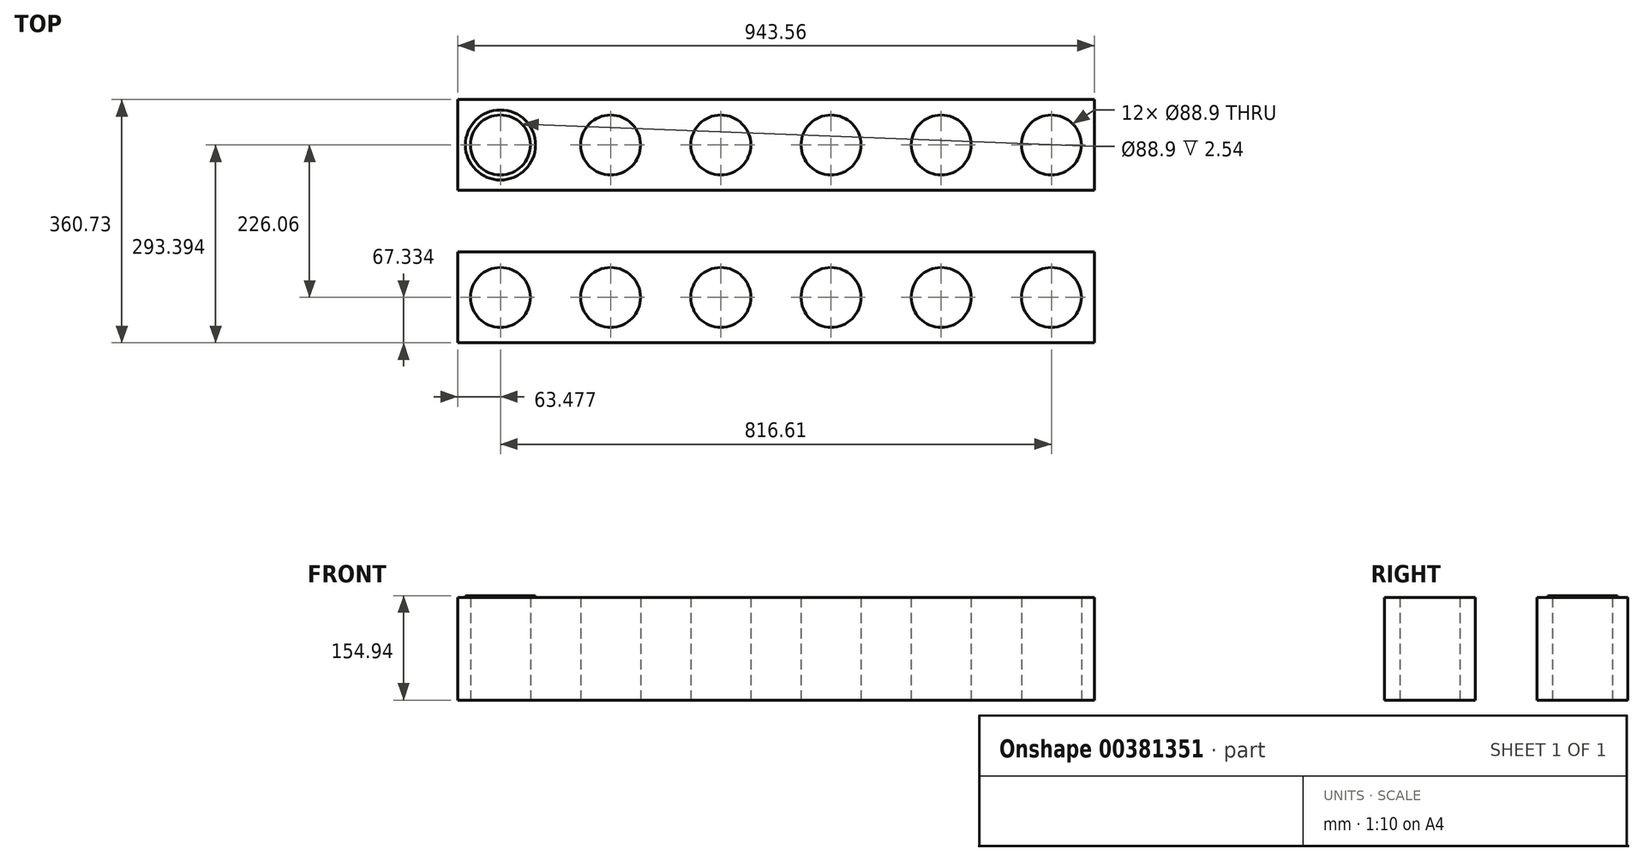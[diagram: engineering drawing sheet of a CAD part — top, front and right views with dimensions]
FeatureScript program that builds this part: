
annotation { "Feature Type Name" : "Feature", "Feature Type Description" : "" }
export const myFeature = defineFeature(function(context is Context, id is Id, definition is map)
    precondition{}
    {
        {
            var Q0;
            Q0=qCreatedBy(makeId("Top.planeOp"),FACE);
            var sketch = newSketch(context, id + "F0", { "sketchPlane" : qUnion([Q0])});
            skCircle(sketch, "E0", {"center": v(-123, 5.68) * mm, "radius": 44.45 * mm});
            skLineSegment(sketch, "E1", {"start": v(-123, 5.68) * mm, "end": v(203.64, 5.68) * mm});
            skCircle(sketch, "E2", {"center": v(40.32, 5.68) * mm, "radius": 44.45 * mm});
            skCircle(sketch, "E3", {"center": v(203.64, 5.68) * mm, "radius": 44.45 * mm});
            skLineSegment(sketch, "E4", {"start": v(366.96, 5.68) * mm, "end": v(640.3, 5.68) * mm});
            skCircle(sketch, "E5", {"center": v(366.96, 5.68) * mm, "radius": 44.45 * mm});
            skCircle(sketch, "E6", {"center": v(530.29, 5.68) * mm, "radius": 44.45 * mm});
            skLineSegment(sketch, "E7", {"start": v(640.3, 5.68) * mm, "end": v(693.6, 5.68) * mm});
            skCircle(sketch, "E8", {"center": v(693.6, 5.68) * mm, "radius": 44.45 * mm});
            skLineSegment(sketch, "E9", {"start": v(203.64, 5.68) * mm, "end": v(366.96, 5.68) * mm});
            skLineSegment(sketch, "E10.bottom", {"start": v(757.08, -61.65) * mm, "end": v(-186.48, -61.65) * mm});
            skLineSegment(sketch, "E10.top", {"start": v(757.08, 73.02) * mm, "end": v(-186.48, 73.02) * mm});
            skLineSegment(sketch, "E10.left", {"start": v(757.08, -61.65) * mm, "end": v(757.08, 73.02) * mm});
            skLineSegment(sketch, "E10.right", {"start": v(-186.48, -61.65) * mm, "end": v(-186.48, 73.02) * mm});
            skPoint(sketch, "E10.middle", {"position": v(285.3, 5.68) * mm});
            skSolve(sketch);
        }
        {
            var Q0;
            Q0 = qSketchRegion(id + "F0", true);
            extrude(context, id + "F1", {"entities" : qUnion([Q0]), "depth" : 152.4 * mm});
        }
        {
            var Q0;
            Q0=makeQuery(id+"F1.opExtrude","SWEPT_BODY",BODY,{"disambiguationData":[OSD([sQuery(id+"F0.wireOp",EDGE,"E0"),sQuery(id+"F0.wireOp",EDGE,"E2"),sQuery(id+"F0.wireOp",EDGE,"E3"),sQuery(id+"F0.wireOp",EDGE,"E5"),sQuery(id+"F0.wireOp",EDGE,"E6"),sQuery(id+"F0.wireOp",EDGE,"E8"),sQuery(id+"F0.wireOp",EDGE,"E10.bottom"),sQuery(id+"F0.wireOp",EDGE,"E10.top"),sQuery(id+"F0.wireOp",EDGE,"E10.left"),sQuery(id+"F0.wireOp",EDGE,"E10.right")])]});
            transform(context, id + "F2", {"entities" : qUnion([Q0]), "transformType" : TransformType.TRANSLATION_3D, "dx" : 0 * mm, "dy" : 226.06 * mm, "dz" : 0 * mm, "makeCopy" : true});
        }
        {
            var Q0;
            Q0=makeQuery(id+"F2.opPattern","COPY",FACE,{"derivedFrom":makeQuery(id+"F1.opExtrude","CAP_FACE",FACE,{"disambiguationData":[OSD([sQuery(id+"F0.wireOp",EDGE,"E0"),sQuery(id+"F0.wireOp",EDGE,"E2"),sQuery(id+"F0.wireOp",EDGE,"E3"),sQuery(id+"F0.wireOp",EDGE,"E5"),sQuery(id+"F0.wireOp",EDGE,"E6"),sQuery(id+"F0.wireOp",EDGE,"E8"),sQuery(id+"F0.wireOp",EDGE,"E10.bottom"),sQuery(id+"F0.wireOp",EDGE,"E10.top"),sQuery(id+"F0.wireOp",EDGE,"E10.left"),sQuery(id+"F0.wireOp",EDGE,"E10.right")])],"isStart":false}),"instanceName":"1"});
            var sketch = newSketch(context, id + "F3", { "sketchPlane" : qUnion([Q0])});
            skCircle(sketch, "E11", {"center": v(-123, 231.74) * mm, "radius": 51.9 * mm});
            skSolve(sketch);
        }
        {
            var Q0;
            Q0=makeQuery(id+"F3.imprint","IMPRINT",FACE,{"disambiguationData":[TD([[makeQuery(id+"F3.imprint","IMPRINT",EDGE,{"derivedFrom":sQuery(id+"F3.wireOp",EDGE,"E11")}),1.0]])]});
            extrude(context, id + "F4", {"entities" : qUnion([Q0]), "depth" : 2.54 * mm});
        }
    });
